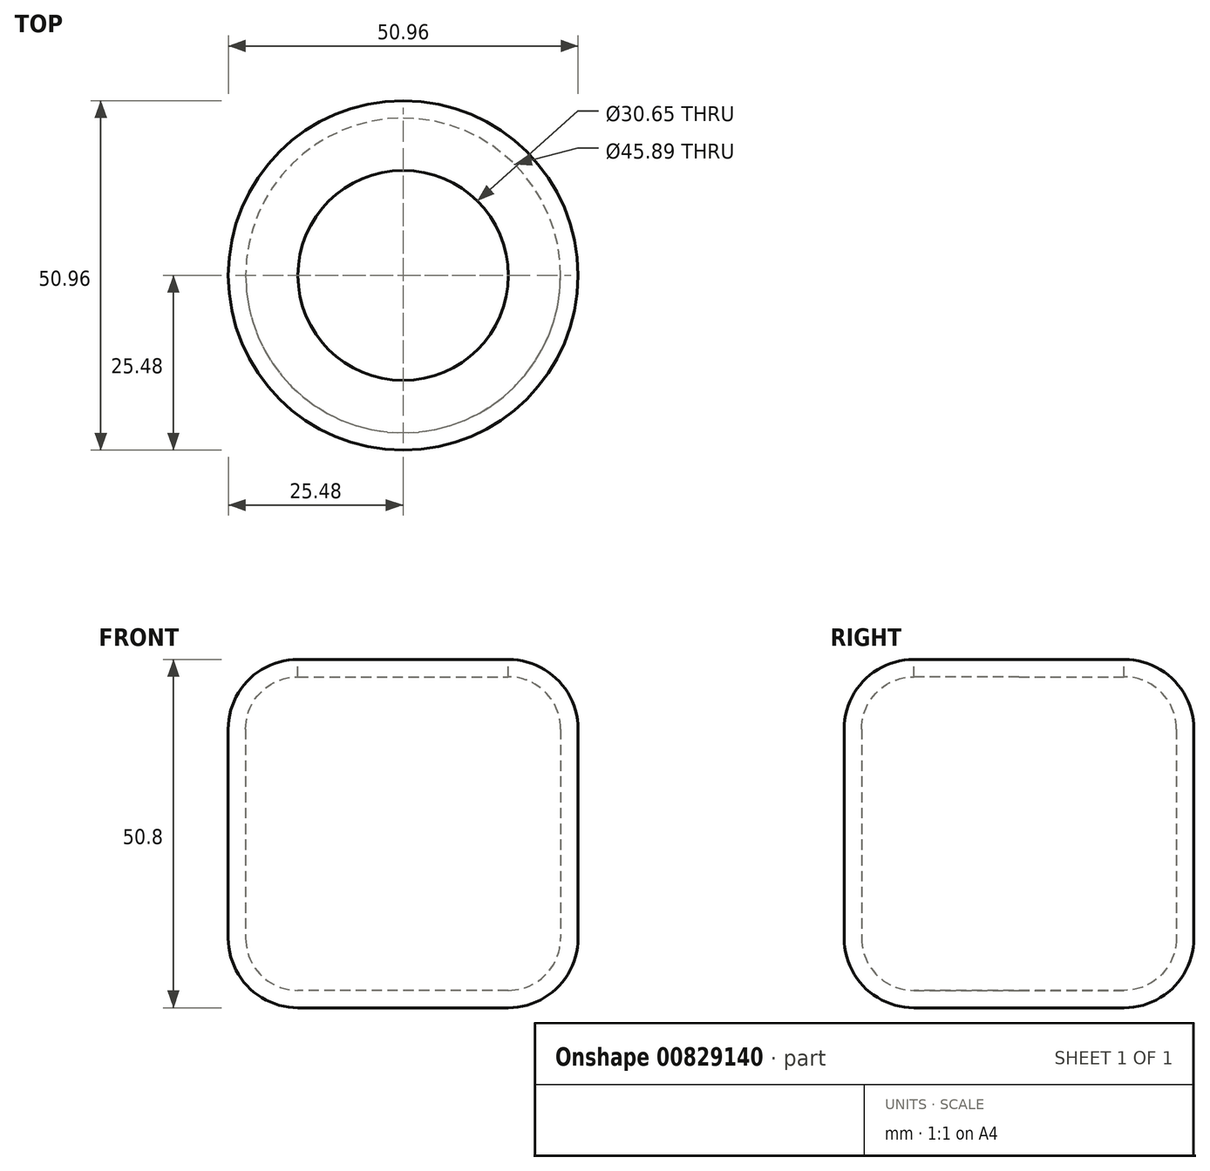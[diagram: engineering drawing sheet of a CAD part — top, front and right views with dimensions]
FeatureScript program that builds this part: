
annotation { "Feature Type Name" : "Feature", "Feature Type Description" : "" }
export const myFeature = defineFeature(function(context is Context, id is Id, definition is map)
    precondition{}
    {
        {
            var Q0;
            Q0=qCreatedBy(makeId("Top.planeOp"),FACE);
            var sketch = newSketch(context, id + "F0", { "sketchPlane" : qUnion([Q0])});
            skCircle(sketch, "E0", {"center": v(0, 0) * mm, "radius": 25.48 * mm});
            skSolve(sketch);
        }
        {
            var Q0;
            Q0 = qSketchRegion(id + "F0", true);
            extrude(context, id + "F1", {"entities" : qUnion([Q0]), "depth" : 50.8 * mm, "offsetDistance" : 25.4 * mm});
        }
        {
            var Q0;
            Q0=makeQuery(id+"F1.opExtrude","CAP_EDGE",EDGE,{"disambiguationData":[OSD([sQuery(id+"F0.wireOp",EDGE,"E0")])],"isStart":true});
            fillet(context, id + "F2", {"entities" : qUnion([Q0]), "radius" : 10.16 * mm, "tangentPropagation" : true, "allowEdgeOverflow" : false});
        }
        {
            var Q0;
            Q0=makeQuery(id+"F1.opExtrude","CAP_EDGE",EDGE,{"disambiguationData":[OSD([sQuery(id+"F0.wireOp",EDGE,"E0")])],"isStart":false});
            var Q1;
            Q1=makeQuery(id+"F1.opExtrude","CAP_FACE",FACE,{"disambiguationData":[OSD([sQuery(id+"F0.wireOp",EDGE,"E0")])],"isStart":false});
            fillet(context, id + "F3", {"entities" : qUnion([Q0, Q1]), "radius" : 10.16 * mm, "tangentPropagation" : true, "allowEdgeOverflow" : false});
        }
        {
            var Q0;
            Q0=makeQuery(id+"F1.opExtrude","CAP_FACE",FACE,{"disambiguationData":[OSD([sQuery(id+"F0.wireOp",EDGE,"E0")])],"isStart":false});
            shell(context, id + "F4", {"entities" : qUnion([Q0]), "thickness" : 2.54 * mm});
        }
    });
